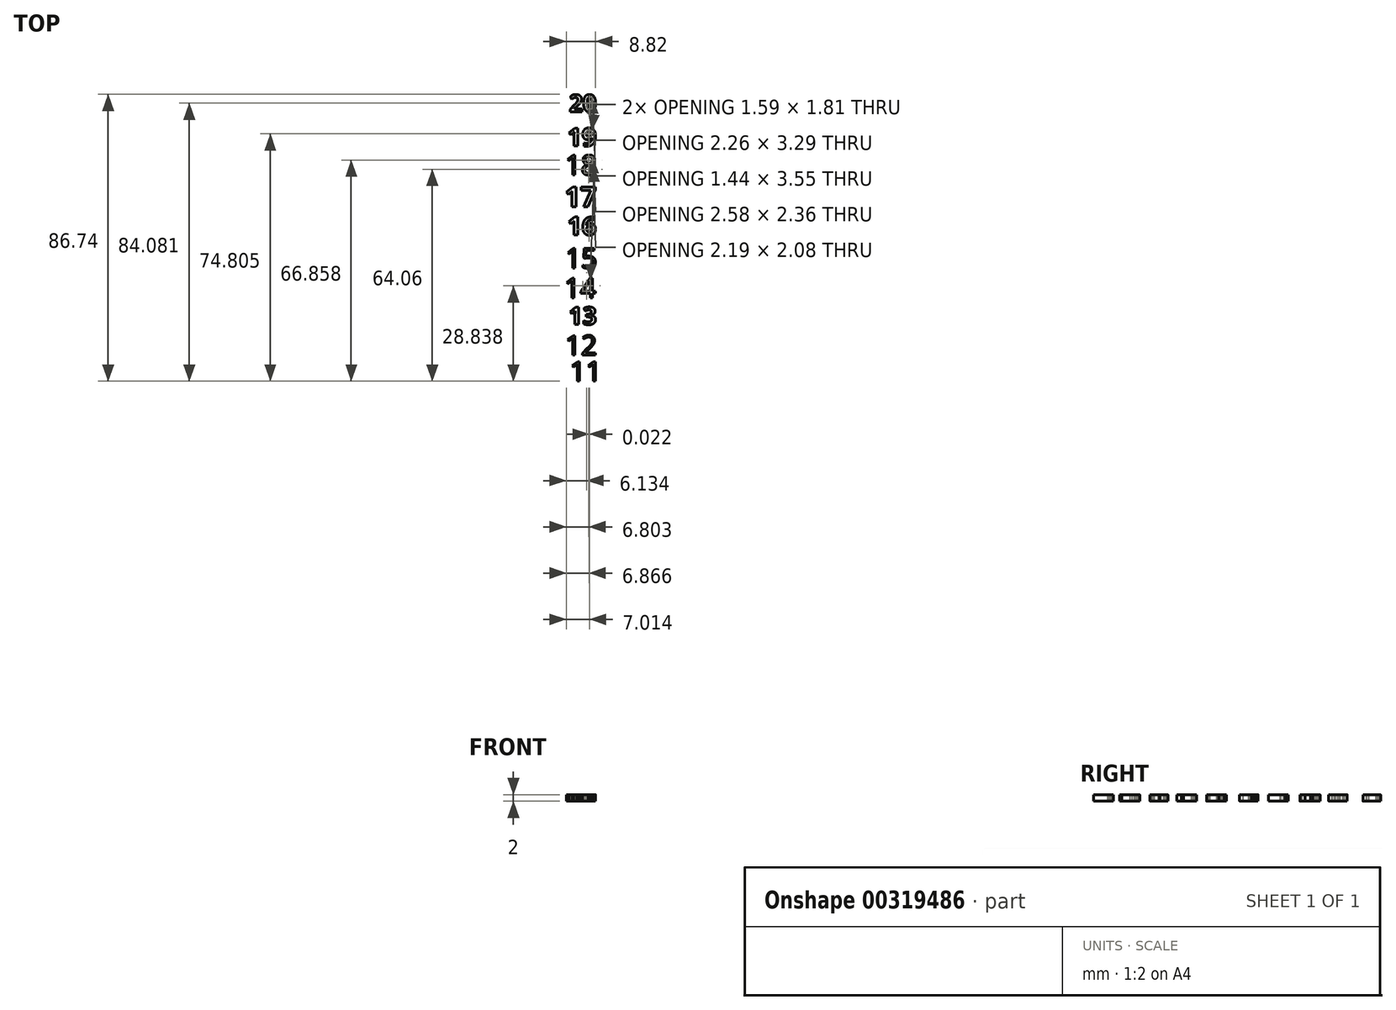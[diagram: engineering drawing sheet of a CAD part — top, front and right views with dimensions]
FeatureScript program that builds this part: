
annotation { "Feature Type Name" : "Feature", "Feature Type Description" : "" }
export const myFeature = defineFeature(function(context is Context, id is Id, definition is map)
    precondition{}
    {
        {
            var Q0;
            Q0=qCreatedBy(makeId("Top.planeOp"),FACE);
            var sketch = newSketch(context, id + "F0", { "sketchPlane" : qUnion([Q0])});
            skText(sketch, "E0", { "text": "11", "fontName": "OpenSans-Regular.ttf"});
            skText(sketch, "E1", { "text": "12", "fontName": "OpenSans-Regular.ttf"});
            skText(sketch, "E2", { "text": "13", "fontName": "OpenSans-Bold.ttf"});
            skText(sketch, "E3", { "text": "14", "fontName": "OpenSans-Regular.ttf"});
            skText(sketch, "E4", { "text": "15", "fontName": "OpenSans-Regular.ttf"});
            skText(sketch, "E5", { "text": "16", "fontName": "OpenSans-Bold.ttf"});
            skText(sketch, "E6", { "text": "17", "fontName": "OpenSans-Bold.ttf"});
            skText(sketch, "E7", { "text": "18", "fontName": "OpenSans-Regular.ttf"});
            skText(sketch, "E8", { "text": "19", "fontName": "OpenSans-Bold.ttf"});
            skText(sketch, "E9", { "text": "20", "fontName": "OpenSans-Bold.ttf"});
            const initialGuessF0  = {"E0": [-0.0166, -0.01486, 1, 0, 0.006], "E1": [-0.018, -0.00697, 1, 0, 0.006], "E2": [-0.01699, 0.0023, 1, 0, 0.0053], "E3": [-0.01829, 0.01035, 1, 0, 0.006], "E4": [-0.01797, 0.01936, 1, 0, 0.006], "E5": [-0.01736, 0.02935, 1, 0, 0.0055], "E6": [-0.01817, 0.03796, 1, 0, 0.006], "E7": [-0.01802, 0.04755, 1, 0, 0.006], "E8": [-0.01733, 0.05626, 1, 0, 0.0055], "E9": [-0.01685, 0.06664, 1, 0, 0.0052]};
            skSetInitialGuess(sketch, initialGuessF0);
            skSolve(sketch);
        }
        {
            var Q0;
            Q0=makeQuery(id+"F0.imprint","IMPRINT",FACE,{"disambiguationData":[TD([[makeQuery(id+"F0.imprint","IMPRINT",EDGE,{"derivedFrom":sQuery(id+"F0.wireOp",EDGE,"E9.sketch_text.stroke-24")}),-1.0]])]});
            var Q1;
            Q1=makeQuery(id+"F0.imprint","IMPRINT",FACE,{"disambiguationData":[TD([[makeQuery(id+"F0.imprint","IMPRINT",EDGE,{"derivedFrom":sQuery(id+"F0.wireOp",EDGE,"E9.sketch_text.stroke-0")}),-1.0]])]});
            var Q2;
            Q2=makeQuery(id+"F0.imprint","IMPRINT",FACE,{"disambiguationData":[TD([[makeQuery(id+"F0.imprint","IMPRINT",EDGE,{"derivedFrom":sQuery(id+"F0.wireOp",EDGE,"E8.sketch_text.stroke-0")}),-1.0]])]});
            var Q3;
            Q3=makeQuery(id+"F0.imprint","IMPRINT",FACE,{"disambiguationData":[TD([[makeQuery(id+"F0.imprint","IMPRINT",EDGE,{"derivedFrom":sQuery(id+"F0.wireOp",EDGE,"E8.sketch_text.stroke-10")}),-1.0]])]});
            var Q4;
            Q4=makeQuery(id+"F0.imprint","IMPRINT",FACE,{"disambiguationData":[TD([[makeQuery(id+"F0.imprint","IMPRINT",EDGE,{"derivedFrom":sQuery(id+"F0.wireOp",EDGE,"E7.sketch_text.stroke-9")}),-1.0]])]});
            var Q5;
            Q5=makeQuery(id+"F0.imprint","IMPRINT",FACE,{"disambiguationData":[TD([[makeQuery(id+"F0.imprint","IMPRINT",EDGE,{"derivedFrom":sQuery(id+"F0.wireOp",EDGE,"E7.sketch_text.stroke-0")}),-1.0]])]});
            var Q6;
            Q6=makeQuery(id+"F0.imprint","IMPRINT",FACE,{"disambiguationData":[TD([[makeQuery(id+"F0.imprint","IMPRINT",EDGE,{"derivedFrom":sQuery(id+"F0.wireOp",EDGE,"E6.sketch_text.stroke-10")}),-1.0]])]});
            var Q7;
            Q7=makeQuery(id+"F0.imprint","IMPRINT",FACE,{"disambiguationData":[TD([[makeQuery(id+"F0.imprint","IMPRINT",EDGE,{"derivedFrom":sQuery(id+"F0.wireOp",EDGE,"E6.sketch_text.stroke-0")}),-1.0]])]});
            var Q8;
            Q8=makeQuery(id+"F0.imprint","IMPRINT",FACE,{"disambiguationData":[TD([[makeQuery(id+"F0.imprint","IMPRINT",EDGE,{"derivedFrom":sQuery(id+"F0.wireOp",EDGE,"E5.sketch_text.stroke-0")}),-1.0]])]});
            var Q9;
            Q9=makeQuery(id+"F0.imprint","IMPRINT",FACE,{"disambiguationData":[TD([[makeQuery(id+"F0.imprint","IMPRINT",EDGE,{"derivedFrom":sQuery(id+"F0.wireOp",EDGE,"E5.sketch_text.stroke-10")}),-1.0]])]});
            var Q10;
            Q10=makeQuery(id+"F0.imprint","IMPRINT",FACE,{"disambiguationData":[TD([[makeQuery(id+"F0.imprint","IMPRINT",EDGE,{"derivedFrom":sQuery(id+"F0.wireOp",EDGE,"E4.sketch_text.stroke-9")}),-1.0]])]});
            var Q11;
            Q11=makeQuery(id+"F0.imprint","IMPRINT",FACE,{"disambiguationData":[TD([[makeQuery(id+"F0.imprint","IMPRINT",EDGE,{"derivedFrom":sQuery(id+"F0.wireOp",EDGE,"E4.sketch_text.stroke-0")}),-1.0]])]});
            var Q12;
            Q12=makeQuery(id+"F0.imprint","IMPRINT",FACE,{"disambiguationData":[TD([[makeQuery(id+"F0.imprint","IMPRINT",EDGE,{"derivedFrom":sQuery(id+"F0.wireOp",EDGE,"E3.sketch_text.stroke-0")}),-1.0]])]});
            var Q13;
            Q13=makeQuery(id+"F0.imprint","IMPRINT",FACE,{"disambiguationData":[TD([[makeQuery(id+"F0.imprint","IMPRINT",EDGE,{"derivedFrom":sQuery(id+"F0.wireOp",EDGE,"E3.sketch_text.stroke-9")}),-1.0]])]});
            var Q14;
            Q14=makeQuery(id+"F0.imprint","IMPRINT",FACE,{"disambiguationData":[TD([[makeQuery(id+"F0.imprint","IMPRINT",EDGE,{"derivedFrom":sQuery(id+"F0.wireOp",EDGE,"E2.sketch_text.stroke-10")}),-1.0]])]});
            var Q15;
            Q15=makeQuery(id+"F0.imprint","IMPRINT",FACE,{"disambiguationData":[TD([[makeQuery(id+"F0.imprint","IMPRINT",EDGE,{"derivedFrom":sQuery(id+"F0.wireOp",EDGE,"E2.sketch_text.stroke-0")}),-1.0]])]});
            var Q16;
            Q16=makeQuery(id+"F0.imprint","IMPRINT",FACE,{"disambiguationData":[TD([[makeQuery(id+"F0.imprint","IMPRINT",EDGE,{"derivedFrom":sQuery(id+"F0.wireOp",EDGE,"E1.sketch_text.stroke-0")}),-1.0]])]});
            var Q17;
            Q17=makeQuery(id+"F0.imprint","IMPRINT",FACE,{"disambiguationData":[TD([[makeQuery(id+"F0.imprint","IMPRINT",EDGE,{"derivedFrom":sQuery(id+"F0.wireOp",EDGE,"E1.sketch_text.stroke-9")}),-1.0]])]});
            var Q18;
            Q18=makeQuery(id+"F0.imprint","IMPRINT",FACE,{"disambiguationData":[TD([[makeQuery(id+"F0.imprint","IMPRINT",EDGE,{"derivedFrom":sQuery(id+"F0.wireOp",EDGE,"E0.sketch_text.stroke-0")}),-1.0]])]});
            var Q19;
            Q19=makeQuery(id+"F0.imprint","IMPRINT",FACE,{"disambiguationData":[TD([[makeQuery(id+"F0.imprint","IMPRINT",EDGE,{"derivedFrom":sQuery(id+"F0.wireOp",EDGE,"E0.sketch_text.stroke-9")}),-1.0]])]});
            extrude(context, id + "F1", {"entities" : qUnion([Q0, Q1, Q2, Q3, Q4, Q5, Q6, Q7, Q8, Q9, Q10, Q11, Q12, Q13, Q14, Q15, Q16, Q17, Q18, Q19]), "depth" : 2 * mm});
        }
    });
